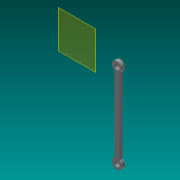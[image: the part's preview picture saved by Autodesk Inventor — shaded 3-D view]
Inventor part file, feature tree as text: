
AUTODESK INVENTOR PART (.ipt)
format: ipt  version: 2013 SP2 (Build 170200200, 200)  size: 88,064 bytes
history: native  units: in
note: dims shown in document units (in); Inventor stores cm internally (conversion verified against a paired STEP export)
features: sheet_metal_op x1, sketch x1, other x1, plane x1
ambient origin geometry x8: Origin, YZ Plane, XZ Plane, XY Plane, X Axis, Y Axis, Z Axis, Center Point
bodies: Solid1 (feature_tree)
feature tree (4):
  sheet_metal_op  "Face1"
  sketch  "Sketch1"  dims[d1=0.228in d2=0.0787in]
  other  "Plate1"
  plane  "Work Plane2"
